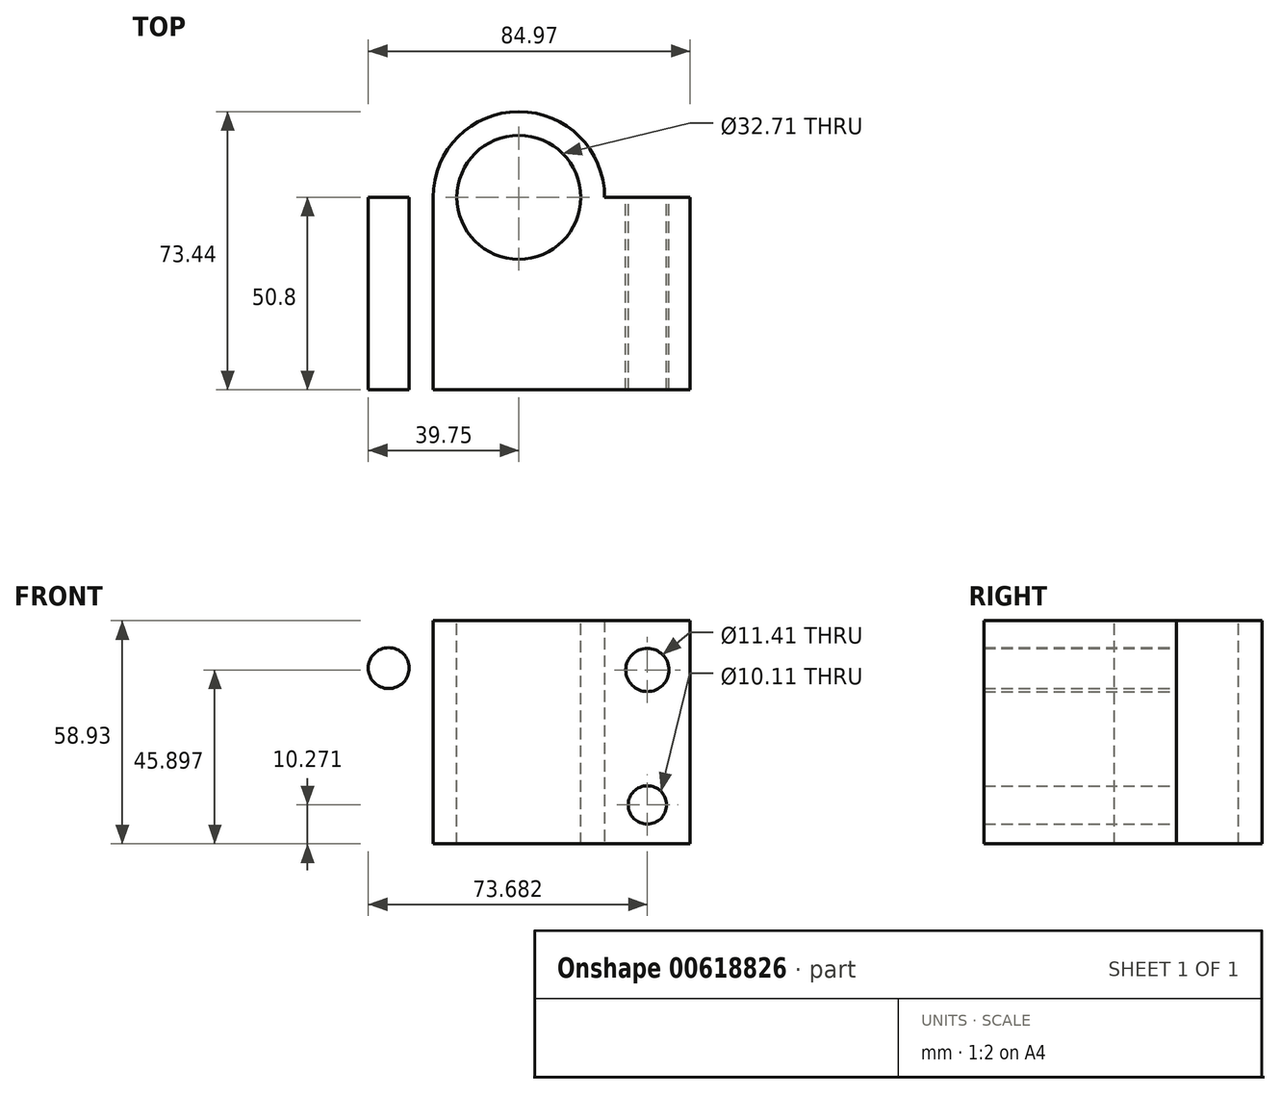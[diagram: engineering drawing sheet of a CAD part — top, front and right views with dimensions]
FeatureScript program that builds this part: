
annotation { "Feature Type Name" : "Feature", "Feature Type Description" : "" }
export const myFeature = defineFeature(function(context is Context, id is Id, definition is map)
    precondition{}
    {
        {
            var Q0;
            Q0=qCreatedBy(makeId("Top.planeOp"),FACE);
            var sketch = newSketch(context, id + "F0", { "sketchPlane" : qUnion([Q0])});
            skLineSegment(sketch, "E0.bottom", {"start": v(45.22, 25.4) * mm, "end": v(22.64, 25.4) * mm});
            skLineSegment(sketch, "E0.top", {"start": v(45.22, -25.4) * mm, "end": v(-45.22, -25.4) * mm});
            skLineSegment(sketch, "E0.left", {"start": v(45.22, 25.4) * mm, "end": v(45.22, -25.4) * mm});
            skLineSegment(sketch, "E0.right", {"start": v(-45.22, 25.4) * mm, "end": v(-45.22, -25.4) * mm});
            skPoint(sketch, "E0.middle", {"position": v(0, 0) * mm});
            skArc(sketch, "E1", {"start": v(22.64, 25.4) * mm, "mid": v(0, 48.04) * mm, "end": v(-22.64, 25.4) * mm});
            skLineSegment(sketch, "E2.trimOffspring", {"start": v(-22.64, 25.4) * mm, "end": v(-45.22, 25.4) * mm});
            skSolve(sketch);
        }
        {
            var Q0;
            Q0=qSketchRegion(id+"F0",true);
            extrude(context, id + "F1", {"entities" : qUnion([Q0]), "depth" : 58.93 * mm, "offsetDistance" : 25.4 * mm});
        }
        {
            var Q0;
            Q0=makeQuery(id+"F1.opExtrude","CAP_FACE",FACE,{"disambiguationData":[OSD([sQuery(id+"F0.wireOp",EDGE,"E0.bottom"),sQuery(id+"F0.wireOp",EDGE,"E0.top"),sQuery(id+"F0.wireOp",EDGE,"E0.left"),sQuery(id+"F0.wireOp",EDGE,"E0.right"),sQuery(id+"F0.wireOp",EDGE,"E1"),sQuery(id+"F0.wireOp",EDGE,"E2.trimOffspring")])],"isStart":false});
            var sketch = newSketch(context, id + "F2", { "sketchPlane" : qUnion([Q0])});
            skCircle(sketch, "E3", {"center": v(0, 25.4) * mm, "radius": 16.36 * mm});
            skSolve(sketch);
        }
        {
            var Q0;
            Q0=makeQuery(id+"F2.imprint","IMPRINT",FACE,{"disambiguationData":[TD([[makeQuery(id+"F2.imprint","IMPRINT",EDGE,{"derivedFrom":sQuery(id+"F2.wireOp",EDGE,"E3")}),1.0]])]});
            extrude(context, id + "F3", {"entities" : qUnion([Q0]), "operationType" : NewBodyOperationType.REMOVE, "oppositeDirection" : true, "depth" : 79.5 * mm, "offsetDistance" : 25.4 * mm});
        }
        {
            var Q0;
            Q0=makeQuery(id+"F1.opExtrude","SWEPT_FACE",FACE,{"disambiguationData":[OSD([sQuery(id+"F0.wireOp",EDGE,"E2.trimOffspring")])]});
            var sketch = newSketch(context, id + "F4", { "sketchPlane" : qUnion([Q0])});
            skCircle(sketch, "E4", {"center": v(33.93, 12.53) * mm, "radius": 5.4 * mm});
            skPoint(sketch, "E4.centerSnap0", {"position": v(33.93, 0) * mm});
            skCircle(sketch, "E5.MirrorC", {"center": v(34.35, 46.4) * mm, "radius": 5.4 * mm});
            skSolve(sketch);
        }
        {
            var Q0;
            Q0=makeQuery(id+"F4.imprint","IMPRINT",FACE,{"disambiguationData":[TD([[makeQuery(id+"F4.imprint","IMPRINT",EDGE,{"derivedFrom":sQuery(id+"F4.wireOp",EDGE,"E4")}),1.0]])]});
            var Q1;
            Q1=makeQuery(id+"F4.imprint","IMPRINT",FACE,{"disambiguationData":[TD([[makeQuery(id+"F4.imprint","IMPRINT",EDGE,{"derivedFrom":sQuery(id+"F4.wireOp",EDGE,"E5.MirrorC")}),-1.0]])]});
            var Q2;
            Q2=sQuery(id+"F4.wireOp",EDGE,"E4");
            var Q3;
            Q3=sQuery(id+"F4.wireOp",EDGE,"E5.MirrorC");
            extrude(context, id + "F5", {"entities" : qUnion([Q0, Q1]), "operationType" : NewBodyOperationType.REMOVE, "surfaceEntities" : qUnion([Q2, Q3]), "oppositeDirection" : true, "depth" : 98.04 * mm, "offsetDistance" : 25.4 * mm});
        }
        {
            var Q0;
            Q0=makeQuery(id+"F1.opExtrude","SWEPT_FACE",FACE,{"disambiguationData":[OSD([sQuery(id+"F0.wireOp",EDGE,"E0.bottom")])]});
            var sketch = newSketch(context, id + "F6", { "sketchPlane" : qUnion([Q0])});
            skPoint(sketch, "E6.centerSnap0", {"position": v(-33.93, 0) * mm});
            skCircle(sketch, "E7", {"center": v(-33.93, 10.27) * mm, "radius": 5.06 * mm});
            skCircle(sketch, "E8", {"center": v(-33.93, 45.9) * mm, "radius": 5.7 * mm});
            skSolve(sketch);
        }
        {
            var Q0;
            Q0=makeQuery(id+"F6.imprint","IMPRINT",FACE,{"disambiguationData":[TD([[makeQuery(id+"F6.imprint","IMPRINT",EDGE,{"derivedFrom":sQuery(id+"F6.wireOp",EDGE,"E7")}),1.0]])]});
            var Q1;
            Q1=makeQuery(id+"F6.imprint","IMPRINT",FACE,{"disambiguationData":[TD([[makeQuery(id+"F6.imprint","IMPRINT",EDGE,{"derivedFrom":sQuery(id+"F6.wireOp",EDGE,"E8")}),1.0]])]});
            extrude(context, id + "F7", {"entities" : qUnion([Q0, Q1]), "operationType" : NewBodyOperationType.REMOVE, "oppositeDirection" : true, "depth" : 93.73 * mm, "offsetDistance" : 25.4 * mm});
        }
    });
